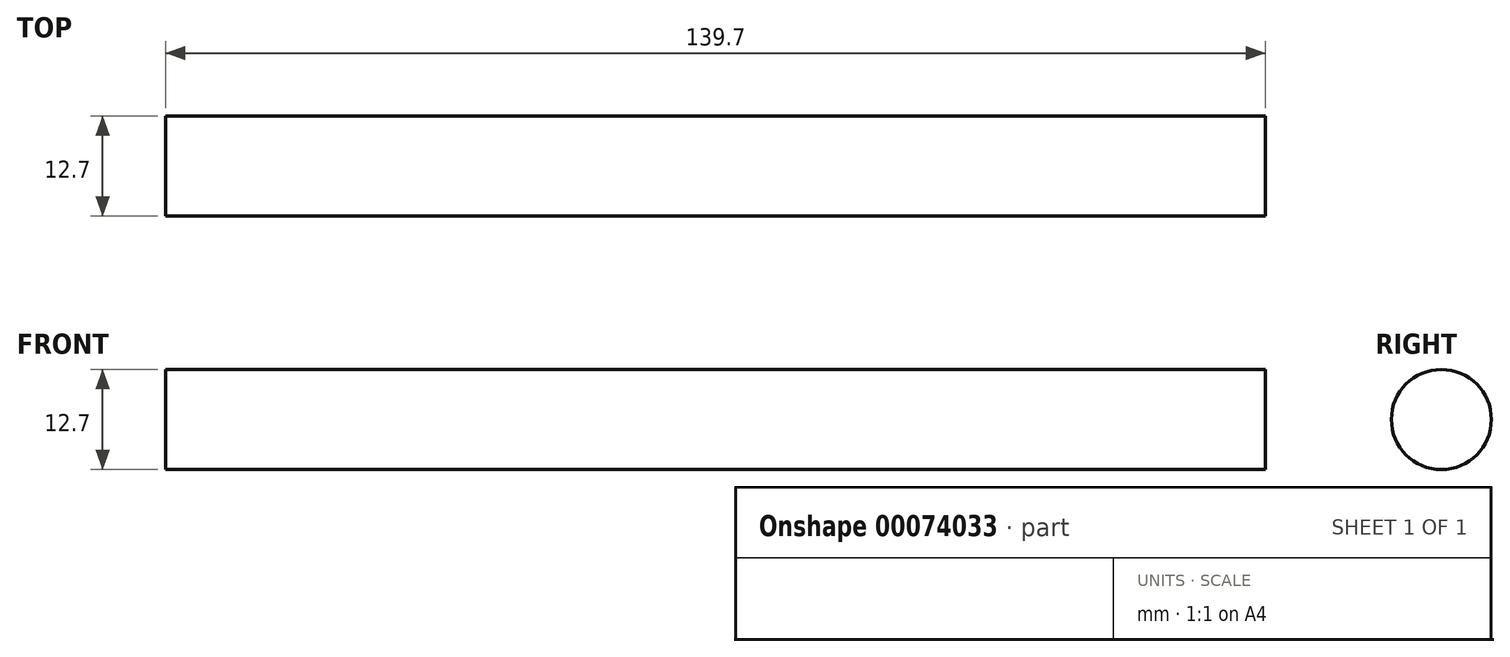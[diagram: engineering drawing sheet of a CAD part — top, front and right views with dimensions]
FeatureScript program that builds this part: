
annotation { "Feature Type Name" : "Feature", "Feature Type Description" : "" }
export const myFeature = defineFeature(function(context is Context, id is Id, definition is map)
    precondition{}
    {
        {
            var Q0;
            Q0=qCreatedBy(makeId("Right.planeOp"),FACE);
            var sketch = newSketch(context, id + "F0", { "sketchPlane" : qUnion([Q0])});
            skCircle(sketch, "E0", {"center": v(0, 0) * mm, "radius": 6.35 * mm});
            skSolve(sketch);
        }
        {
            var Q0;
            Q0=makeQuery(id+"F0.imprint","IMPRINT",FACE,{"disambiguationData":[TD([[makeQuery(id+"F0.imprint","IMPRINT",EDGE,{"derivedFrom":sQuery(id+"F0.wireOp",EDGE,"E0")}),1.0]])]});
            extrude(context, id + "F1", {"entities" : qUnion([Q0]), "depth" : 139.7 * mm, "symmetric" : true});
        }
    });
